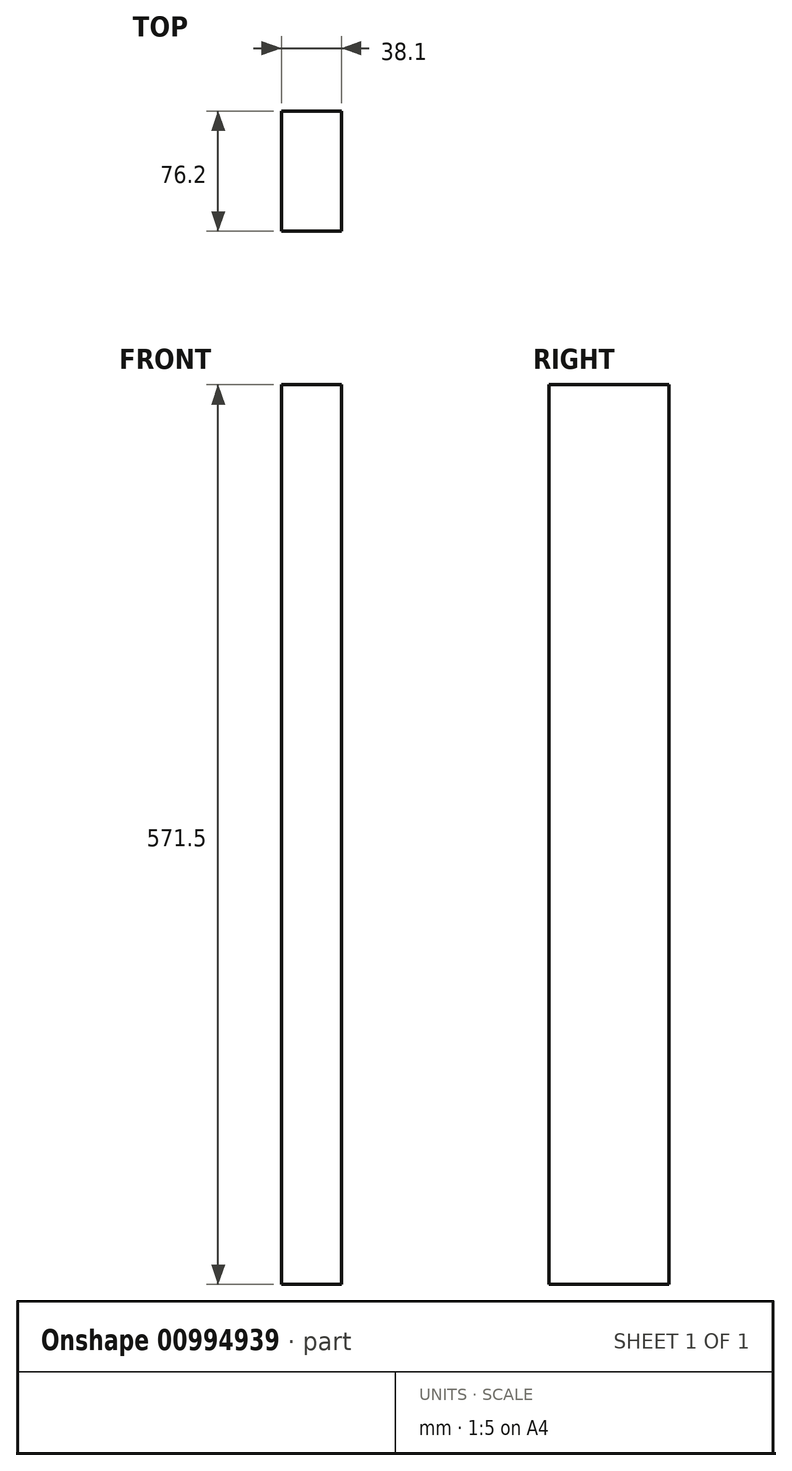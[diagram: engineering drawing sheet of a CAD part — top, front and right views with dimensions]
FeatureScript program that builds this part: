
annotation { "Feature Type Name" : "Feature", "Feature Type Description" : "" }
export const myFeature = defineFeature(function(context is Context, id is Id, definition is map)
    precondition{}
    {
        {
            var Q0;
            Q0=qCreatedBy(makeId("Front.planeOp"),FACE);
            var sketch = newSketch(context, id + "F0", { "sketchPlane" : qUnion([Q0])});
            skLineSegment(sketch, "E0.bottom", {"start": v(-19.05, 0) * mm, "end": v(19.05, 0) * mm});
            skLineSegment(sketch, "E0.top", {"start": v(-19.05, 571.5) * mm, "end": v(19.05, 571.5) * mm});
            skLineSegment(sketch, "E0.left", {"start": v(-19.05, 0) * mm, "end": v(-19.05, 571.5) * mm});
            skLineSegment(sketch, "E0.right", {"start": v(19.05, 0) * mm, "end": v(19.05, 571.5) * mm});
            skSolve(sketch);
        }
        {
            var Q0;
            Q0 = qSketchRegion(id + "F0", true);
            extrude(context, id + "F1", {"entities" : qUnion([Q0]), "oppositeDirection" : true, "depth" : 76.2 * mm, "offsetDistance" : 25.4 * mm});
        }
    });
